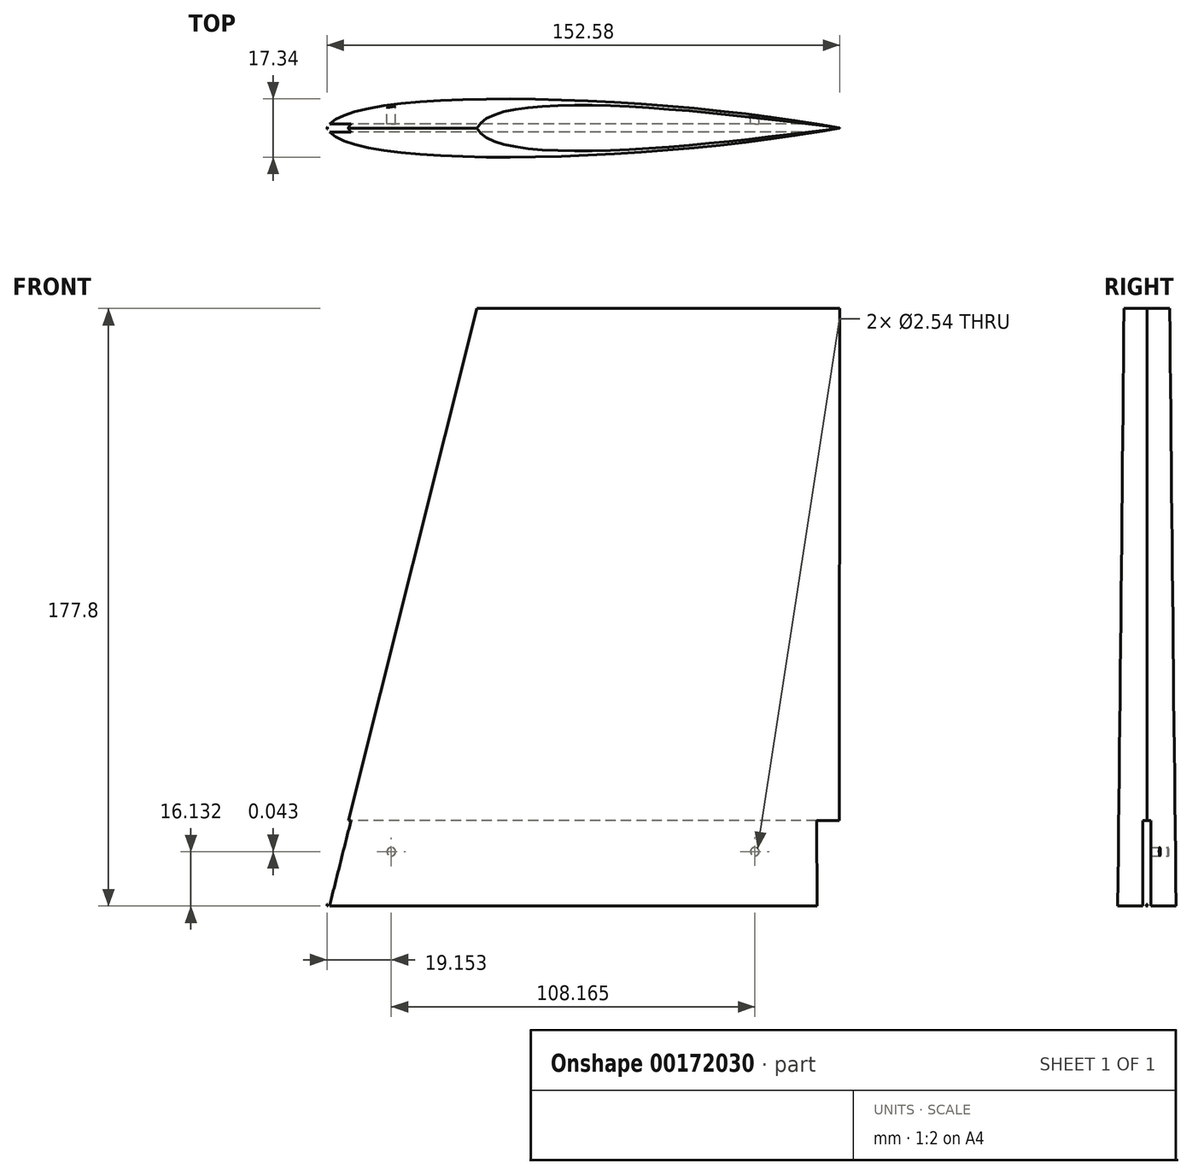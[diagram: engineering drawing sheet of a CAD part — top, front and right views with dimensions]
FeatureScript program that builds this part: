
annotation { "Feature Type Name" : "Feature", "Feature Type Description" : "" }
export const myFeature = defineFeature(function(context is Context, id is Id, definition is map)
    precondition{}
    {
        {
            var Q0;
            Q0=qCreatedBy(makeId("Top.planeOp"),FACE);
            var sketch = newSketch(context, id + "F0", { "sketchPlane" : qUnion([Q0])});
            skFitSpline(sketch, "E0", {"points": [v(-76.34, 0) * mm, v(76.06, 0) * mm], "startDerivative": vector(16.92, 39.6) * mm, "endDerivative": vector(152.37, -29.39) * mm});
            skFitSpline(sketch, "E1.MirrorCS", {"points": [v(-76.34, 0) * mm, v(76.06, 0) * mm], "startDerivative": vector(16.92, -39.6) * mm, "endDerivative": vector(152.37, 29.39) * mm});
            skSolve(sketch);
        }
        {
            var Q0;
            Q0=qCreatedBy(makeId("Top.planeOp"),FACE);
            cPlane(context, id + "F1", {"entities" : qUnion([Q0]), "cplaneType" : CPlaneType.OFFSET, "offset" : 177.8 * mm, "width" : 152.4 * mm, "height" : 152.4 * mm});
        }
        {
            var Q0;
            Q0=qCreatedBy(id+"F1.planeOp",FACE);
            var sketch = newSketch(context, id + "F2", { "sketchPlane" : qUnion([Q0])});
            skFitSpline(sketch, "E2", {"points": [v(-31.71, 0) * mm, v(76.24, 0) * mm], "startDerivative": vector(17.63, 37.9) * mm, "endDerivative": vector(107.75, -14.05) * mm});
            skFitSpline(sketch, "E3.MirrorCS", {"points": [v(-31.71, 0) * mm, v(76.24, 0) * mm], "startDerivative": vector(17.63, -37.9) * mm, "endDerivative": vector(107.75, 14.05) * mm});
            skSolve(sketch);
        }
        {
            var Q0;
            Q0=makeQuery(id+"F0.imprint","IMPRINT",FACE,{"disambiguationData":[TD([[makeQuery(id+"F0.imprint","IMPRINT",EDGE,{"derivedFrom":sQuery(id+"F0.wireOp",EDGE,"E0")}),-1.0]])]});
            var Q1;
            Q1=makeQuery(id+"F2.imprint","IMPRINT",FACE,{"disambiguationData":[TD([[makeQuery(id+"F2.imprint","IMPRINT",EDGE,{"derivedFrom":sQuery(id+"F2.wireOp",EDGE,"E2")}),-1.0]])]});
            loft(context, id + "F3", {"sheetProfilesArray" : [{ "sheetProfileEntities" : qUnion([Q0]) }, { "sheetProfileEntities" : qUnion([Q1]) }]});
        }
        {
            var Q0;
            Q0=qCreatedBy(makeId("Top.planeOp"),FACE);
            var sketch = newSketch(context, id + "F4", { "sketchPlane" : qUnion([Q0])});
            skLineSegment(sketch, "E4.bottom", {"start": v(76.2, -1.18) * mm, "end": v(-76.2, -1.18) * mm});
            skLineSegment(sketch, "E4.top", {"start": v(76.2, 1.18) * mm, "end": v(-76.2, 1.18) * mm});
            skLineSegment(sketch, "E4.left", {"start": v(76.2, -1.18) * mm, "end": v(76.2, 1.18) * mm});
            skLineSegment(sketch, "E4.right", {"start": v(-76.2, -1.18) * mm, "end": v(-76.2, 1.18) * mm});
            skPoint(sketch, "E4.middle", {"position": v(0, 0) * mm});
            skSolve(sketch);
        }
        {
            var Q0;
            Q0 = qSketchRegion(id + "F4", true);
            extrude(context, id + "F5", {"entities" : qUnion([Q0]), "operationType" : NewBodyOperationType.REMOVE, "depth" : 25.4 * mm});
        }
        {
            var Q0;
            Q0=qCreatedBy(makeId("Front.planeOp"),FACE);
            var sketch = newSketch(context, id + "F6", { "sketchPlane" : qUnion([Q0])});
            skPoint(sketch, "E5", {"position": v(-57.19, 16.13) * mm});
            skPoint(sketch, "E6", {"position": v(-50.84, 16.13) * mm});
            skPoint(sketch, "E7", {"position": v(50.98, 16.18) * mm});
            skPoint(sketch, "E8", {"position": v(57.33, 16.18) * mm});
            skSolve(sketch);
        }
        {
            var Q0;
            Q0=sQuery(id+"F6.wireOp",VERTEX,"E5");
            var Q1;
            Q1=sQuery(id+"F6.wireOp",VERTEX,"E7");
            var Q2;
            Q2=makeQuery(id+"F5.boolean.opBoolean","SPLIT",BODY,{"disambiguationData":[OD(1.0)],"derivedFrom":makeQuery(id+"F3.opLoft","SWEPT_BODY",BODY,{"disambiguationData":[OSD([makeQuery(id+"F0.imprint","IMPRINT",FACE,{"disambiguationData":[TD([[makeQuery(id+"F0.imprint","IMPRINT",EDGE,{"derivedFrom":sQuery(id+"F0.wireOp",EDGE,"E0")}),-1.0]])]}),makeQuery(id+"F2.imprint","IMPRINT",FACE,{"disambiguationData":[TD([[makeQuery(id+"F2.imprint","IMPRINT",EDGE,{"derivedFrom":sQuery(id+"F2.wireOp",EDGE,"E2")}),-1.0]])]})])]})});
            hole(context, id + "F7", {"style" : HoleStyle.SIMPLE, "endStyle" : HoleEndStyle.BLIND, "holeDiameter" : 2.54 * mm, "holeDepth" : 38.1 * mm, "locations" : qUnion([Q0, Q1]), "scope" : qUnion([Q2]), "startStyle" : HoleStartStyle.PART});
        }
    });
